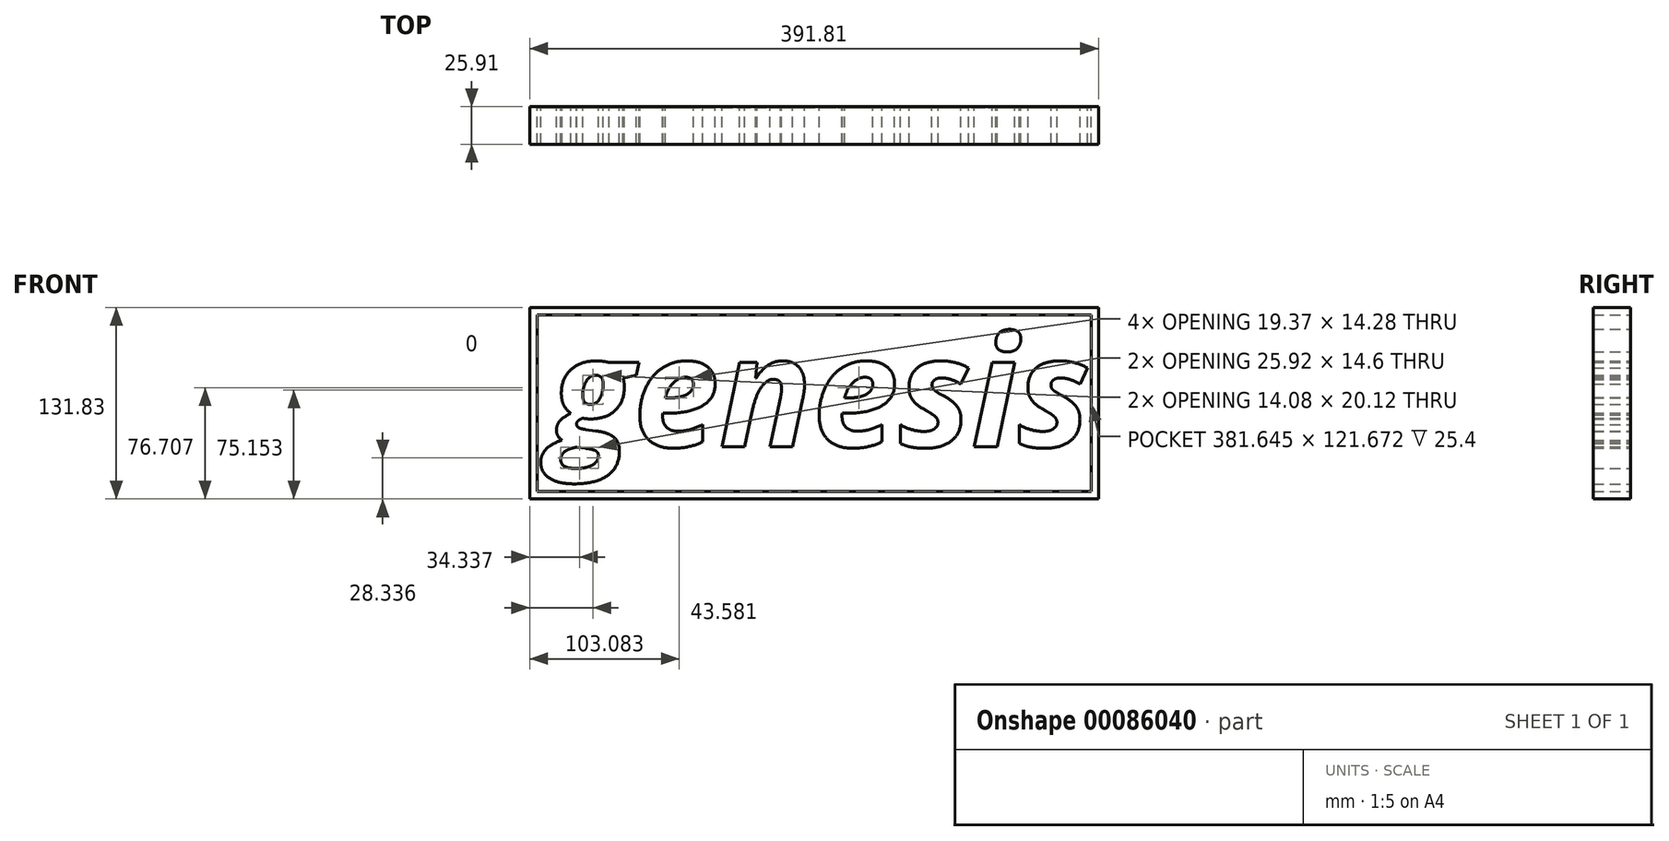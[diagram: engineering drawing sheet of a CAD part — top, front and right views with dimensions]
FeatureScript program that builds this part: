
annotation { "Feature Type Name" : "Feature", "Feature Type Description" : "" }
export const myFeature = defineFeature(function(context is Context, id is Id, definition is map)
    precondition{}
    {
        {
            var Q0;
            Q0=qCreatedBy(makeId("Front.planeOp"),FACE);
            var sketch = newSketch(context, id + "F0", { "sketchPlane" : qUnion([Q0])});
            skText(sketch, "E0", { "text": "genesis", "fontName": "OpenSans-BoldItalic.ttf"});
            const initialGuessF0  = {"E0": [-0.06021, -0.03198, 1, 0, 0.07661]};
            skSetInitialGuess(sketch, initialGuessF0);
            skSolve(sketch);
        }
        {
            var Q0;
            Q0 = qSketchRegion(id + "F0", true);
            extrude(context, id + "F1", {"entities" : qUnion([Q0]), "depth" : 25.4 * mm});
        }
        {
            var Q0;
            Q0 = qSketchRegion(id + "F0", true);
            extrude(context, id + "F2", {"entities" : qUnion([Q0]), "depth" : 25.4 * mm});
        }
        {
            var Q0;
            Q0=makeQuery(id+"F1.opExtrude","CAP_FACE",FACE,{"disambiguationData":[OSD([sQuery(id+"F0.wireOp",EDGE,"E0.sketch_text.stroke-65"),sQuery(id+"F0.wireOp",EDGE,"E0.sketch_text.stroke-66"),sQuery(id+"F0.wireOp",EDGE,"E0.sketch_text.stroke-67"),sQuery(id+"F0.wireOp",EDGE,"E0.sketch_text.stroke-68"),sQuery(id+"F0.wireOp",EDGE,"E0.sketch_text.stroke-69"),sQuery(id+"F0.wireOp",EDGE,"E0.sketch_text.stroke-70"),sQuery(id+"F0.wireOp",EDGE,"E0.sketch_text.stroke-71"),sQuery(id+"F0.wireOp",EDGE,"E0.sketch_text.stroke-72"),sQuery(id+"F0.wireOp",EDGE,"E0.sketch_text.stroke-73"),sQuery(id+"F0.wireOp",EDGE,"E0.sketch_text.stroke-74"),sQuery(id+"F0.wireOp",EDGE,"E0.sketch_text.stroke-75"),sQuery(id+"F0.wireOp",EDGE,"E0.sketch_text.stroke-76"),sQuery(id+"F0.wireOp",EDGE,"E0.sketch_text.stroke-77"),sQuery(id+"F0.wireOp",EDGE,"E0.sketch_text.stroke-78"),sQuery(id+"F0.wireOp",EDGE,"E0.sketch_text.stroke-79"),sQuery(id+"F0.wireOp",EDGE,"E0.sketch_text.stroke-80"),sQuery(id+"F0.wireOp",EDGE,"E0.sketch_text.stroke-81")])],"isStart":true});
            var sketch = newSketch(context, id + "F3", { "sketchPlane" : qUnion([Q0])});
            skLineSegment(sketch, "E1.bottom", {"start": v(-318.02, 63.9) * mm, "end": v(73.79, 63.9) * mm});
            skLineSegment(sketch, "E1.top", {"start": v(-318.02, -67.93) * mm, "end": v(73.79, -67.93) * mm});
            skLineSegment(sketch, "E1.left", {"start": v(-318.02, 63.9) * mm, "end": v(-318.02, -67.93) * mm});
            skLineSegment(sketch, "E1.right", {"start": v(73.79, 63.9) * mm, "end": v(73.79, -67.93) * mm});
            skSolve(sketch);
        }
        {
            var Q0;
            Q0 = qSketchRegion(id + "F3", true);
            extrude(context, id + "F4", {"entities" : qUnion([Q0]), "depth" : 0.5 * mm});
        }
        {
            var Q0;
            Q0=makeQuery(id+"F4.opExtrude","CAP_FACE",FACE,{"disambiguationData":[OSD([sQuery(id+"F3.wireOp",EDGE,"E1.bottom"),sQuery(id+"F3.wireOp",EDGE,"E1.top"),sQuery(id+"F3.wireOp",EDGE,"E1.left"),sQuery(id+"F3.wireOp",EDGE,"E1.right")])],"isStart":true});
            var sketch = newSketch(context, id + "F5", { "sketchPlane" : qUnion([Q0])});
            skLineSegment(sketch, "E2.bottom", {"start": v(-73.79, 63.9) * mm, "end": v(318.02, 63.9) * mm});
            skLineSegment(sketch, "E2.top", {"start": v(-73.79, 58.82) * mm, "end": v(318.02, 58.82) * mm});
            skLineSegment(sketch, "E2.left", {"start": v(-73.79, 63.9) * mm, "end": v(-73.79, 58.82) * mm});
            skLineSegment(sketch, "E2.right", {"start": v(318.02, 63.9) * mm, "end": v(318.02, 58.82) * mm});
            skLineSegment(sketch, "E3.bottom", {"start": v(312.94, 58.82) * mm, "end": v(318.02, 58.82) * mm});
            skLineSegment(sketch, "E3.top", {"start": v(312.94, -67.93) * mm, "end": v(318.02, -67.93) * mm});
            skLineSegment(sketch, "E3.left", {"start": v(312.94, 58.82) * mm, "end": v(312.94, -67.93) * mm});
            skLineSegment(sketch, "E3.right", {"start": v(318.02, 58.82) * mm, "end": v(318.02, -67.93) * mm});
            skLineSegment(sketch, "E4.bottom", {"start": v(318.02, -62.85) * mm, "end": v(-73.79, -62.85) * mm});
            skLineSegment(sketch, "E4.top", {"start": v(318.02, -67.93) * mm, "end": v(-73.79, -67.93) * mm});
            skLineSegment(sketch, "E4.left", {"start": v(318.02, -62.85) * mm, "end": v(318.02, -67.93) * mm});
            skLineSegment(sketch, "E4.right", {"start": v(-73.79, -62.85) * mm, "end": v(-73.79, -67.93) * mm});
            skLineSegment(sketch, "E5.bottom", {"start": v(-68.7, -67.93) * mm, "end": v(-73.79, -67.93) * mm});
            skLineSegment(sketch, "E5.top", {"start": v(-68.7, 63.9) * mm, "end": v(-73.79, 63.9) * mm});
            skLineSegment(sketch, "E5.left", {"start": v(-68.7, -67.93) * mm, "end": v(-68.7, 63.9) * mm});
            skLineSegment(sketch, "E5.right", {"start": v(-73.79, -67.93) * mm, "end": v(-73.79, 63.9) * mm});
            skSolve(sketch);
        }
        {
            var Q0;
            Q0 = qSketchRegion(id + "F5", true);
            extrude(context, id + "F6", {"entities" : qUnion([Q0]), "operationType" : NewBodyOperationType.ADD, "depth" : 25.4 * mm});
        }
    });
